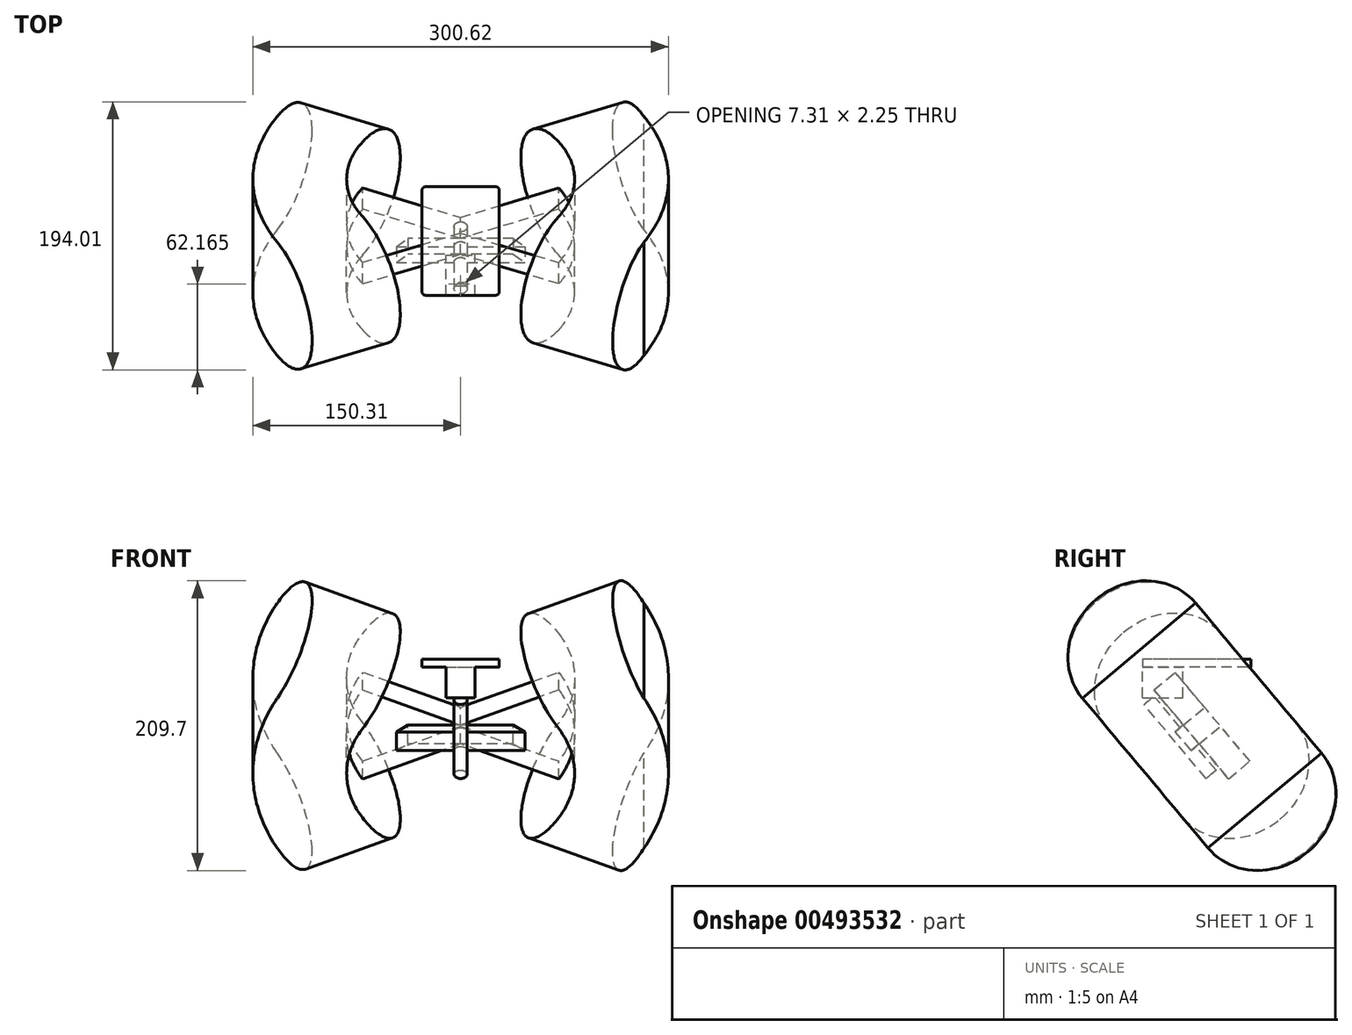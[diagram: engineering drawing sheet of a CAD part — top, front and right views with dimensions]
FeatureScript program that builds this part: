
annotation { "Feature Type Name" : "Feature", "Feature Type Description" : "" }
export const myFeature = defineFeature(function(context is Context, id is Id, definition is map)
    precondition{}
    {
        {
            var Q0;
            Q0=qCreatedBy(makeId("Top.planeOp"),FACE);
            var sketch = newSketch(context, id + "F0", { "sketchPlane" : qUnion([Q0])});
            skLineSegment(sketch, "E0.bottom", {"start": v(-25.4, 39.27) * mm, "end": v(25.4, 39.27) * mm});
            skLineSegment(sketch, "E0.top", {"start": v(-25.4, -39.27) * mm, "end": v(25.4, -39.27) * mm});
            skLineSegment(sketch, "E0.left", {"start": v(-27.94, 36.73) * mm, "end": v(-27.94, -36.73) * mm});
            skLineSegment(sketch, "E0.right", {"start": v(27.94, 36.73) * mm, "end": v(27.94, -36.73) * mm});
            skLineSegment(sketch, "E1", {"start": v(-27.94, 39.27) * mm, "end": v(27.94, -39.27) * mm, "construction": true});
            skPoint(sketch, "E2.visualSharp", {"position": v(-27.94, 39.27) * mm});
            skArc(sketch, "E2.filletArc", {"start": v(-25.4, 39.27) * mm, "mid": v(-27.2, 38.52) * mm, "end": v(-27.94, 36.73) * mm});
            skPoint(sketch, "E3.visualSharp", {"position": v(27.94, 39.27) * mm});
            skArc(sketch, "E3.filletArc", {"start": v(27.94, 36.73) * mm, "mid": v(27.2, 38.52) * mm, "end": v(25.4, 39.27) * mm});
            skPoint(sketch, "E4.visualSharp", {"position": v(27.94, -39.27) * mm});
            skArc(sketch, "E4.filletArc", {"start": v(25.4, -39.27) * mm, "mid": v(27.2, -38.52) * mm, "end": v(27.94, -36.73) * mm});
            skPoint(sketch, "E5.visualSharp", {"position": v(-27.94, -39.27) * mm});
            skArc(sketch, "E5.filletArc", {"start": v(-27.94, -36.73) * mm, "mid": v(-27.2, -38.52) * mm, "end": v(-25.4, -39.27) * mm});
            skSolve(sketch);
        }
        {
            var Q0;
            Q0 = qSketchRegion(id + "F0", true);
            extrude(context, id + "F1", {"entities" : qUnion([Q0]), "depth" : 5.64 * mm, "offsetDistance" : 25.4 * mm});
        }
        {
            var Q0;
            Q0=makeQuery(id+"F1.opExtrude","CAP_FACE",FACE,{"disambiguationData":[OSD([sQuery(id+"F0.wireOp",EDGE,"E0.bottom"),sQuery(id+"F0.wireOp",EDGE,"E0.top"),sQuery(id+"F0.wireOp",EDGE,"E0.left"),sQuery(id+"F0.wireOp",EDGE,"E0.right"),sQuery(id+"F0.wireOp",EDGE,"E2.filletArc"),sQuery(id+"F0.wireOp",EDGE,"E3.filletArc"),sQuery(id+"F0.wireOp",EDGE,"E4.filletArc"),sQuery(id+"F0.wireOp",EDGE,"E5.filletArc")])],"isStart":true});
            var sketch = newSketch(context, id + "F2", { "sketchPlane" : qUnion([Q0])});
            skLineSegment(sketch, "E6.bottom", {"start": v(-10.49, 39.27) * mm, "end": v(10.49, 39.27) * mm});
            skLineSegment(sketch, "E6.top", {"start": v(-10.49, 10.06) * mm, "end": v(10.49, 10.06) * mm});
            skLineSegment(sketch, "E6.left", {"start": v(-10.49, 39.27) * mm, "end": v(-10.49, 10.06) * mm});
            skLineSegment(sketch, "E6.right", {"start": v(10.49, 39.27) * mm, "end": v(10.49, 10.06) * mm});
            skLineSegment(sketch, "E7", {"start": v(0, 0) * mm, "end": v(0, 10.06) * mm, "construction": true});
            skSolve(sketch);
        }
        {
            var Q0;
            Q0 = qSketchRegion(id + "F2", true);
            extrude(context, id + "F3", {"entities" : qUnion([Q0]), "operationType" : NewBodyOperationType.ADD, "depth" : 22.22 * mm, "offsetDistance" : 25.4 * mm});
        }
        {
            var Q0;
            Q0=qCreatedBy(makeId("Right.planeOp"),FACE);
            var sketch = newSketch(context, id + "F4", { "sketchPlane" : qUnion([Q0])});
            skLineSegment(sketch, "E8", {"start": v(-39.27, -18.6) * mm, "end": v(10.3, -77.67) * mm, "construction": true});
            skLineSegment(sketch, "E9", {"start": v(-38.23, 0) * mm, "end": v(-38.23, -19.84) * mm, "construction": true});
            skLineSegment(sketch, "E10", {"start": v(-38.23, -19.84) * mm, "end": v(-39.27, -19.84) * mm, "construction": true});
            skLineSegment(sketch, "E11", {"start": v(-30.97, -21.12) * mm, "end": v(-38.23, -27.2) * mm, "construction": true});
            skPoint(sketch, "E12", {"position": v(-34.6, -24.16) * mm});
            skPoint(sketch, "E13", {"position": v(-15.5, -46.93) * mm});
            skPoint(sketch, "E14", {"position": v(-4.07, -60.55) * mm});
            skPoint(sketch, "E15", {"position": v(-9.78, -53.74) * mm});
            skLineSegment(sketch, "E16", {"start": v(-9.78, -53.74) * mm, "end": v(17.1, -31.18) * mm, "construction": true});
            skSolve(sketch);
        }
        {
            var Q0;
            Q0=sQuery(id+"F4.wireOp",EDGE,"E11");
            cPoint(context, id + "F5", {"entities" : qUnion([Q0]), "parameter" : 0.5});
        }
        {
            var Q0;
            Q0 = qCreatedBy(id + "F5" ,VERTEX);
            var Q1;
            Q1=sQuery(id+"F4.wireOp",EDGE,"E8");
            cPlane(context, id + "F6", {"entities" : qUnion([Q0, Q1]), "cplaneType" : CPlaneType.LINE_POINT, "offset" : 25.4 * mm, "width" : 152.4 * mm, "height" : 152.4 * mm});
        }
        {
            var Q0;
            Q0=qCreatedBy(id+"F6.planeOp",FACE);
            var sketch = newSketch(context, id + "F7", { "sketchPlane" : qUnion([Q0])});
            skCircle(sketch, "E17", {"center": v(0, 42.03) * mm, "radius": 4.74 * mm});
            skSolve(sketch);
        }
        {
            var Q0;
            Q0 = qSketchRegion(id + "F7", true);
            var Q1;
            Q1=sQuery(id+"F4.wireOp",VERTEX,"E8.end");
            extrude(context, id + "F8", {"entities" : qUnion([Q0]), "operationType" : NewBodyOperationType.ADD, "endBound" : BoundingType.UP_TO_VERTEX, "depth" : 25.4 * mm, "endBoundEntityVertex" : qUnion([Q1]), "offsetDistance" : 25.4 * mm});
        }
        {
            var Q0;
            Q0=sQuery(id+"F4.wireOp",EDGE,"E8");
            var Q1;
            Q1=sQuery(id+"F4.wireOp",VERTEX,"E13");
            cPlane(context, id + "F9", {"entities" : qUnion([Q0, Q1]), "cplaneType" : CPlaneType.LINE_POINT, "offset" : 25.4 * mm, "width" : 152.4 * mm, "height" : 152.4 * mm});
        }
        {
            var Q0;
            Q0=qCreatedBy(id+"F9.planeOp",FACE);
            var sketch = newSketch(context, id + "F10", { "sketchPlane" : qUnion([Q0])});
            skLineSegment(sketch, "E18", {"start": v(-92, 14.45) * mm, "end": v(92, 14.45) * mm});
            skLineSegment(sketch, "E19", {"start": v(92, 14.45) * mm, "end": v(92, 34.47) * mm});
            skLineSegment(sketch, "E20", {"start": v(92, 34.47) * mm, "end": v(-92, 34.47) * mm});
            skLineSegment(sketch, "E21", {"start": v(-92, 34.47) * mm, "end": v(-92, 14.45) * mm});
            skLineSegment(sketch, "E22", {"start": v(0, 34.47) * mm, "end": v(0, 0) * mm, "construction": true});
            skLineSegment(sketch, "E23", {"start": v(-46.47, 42.03) * mm, "end": v(-38.1, 34.47) * mm});
            skLineSegment(sketch, "E24", {"start": v(-46.47, 42.03) * mm, "end": v(46.47, 42.03) * mm});
            skLineSegment(sketch, "E25", {"start": v(38.1, 34.47) * mm, "end": v(46.47, 42.03) * mm});
            skSolve(sketch);
        }
        {
            var Q0;
            Q0 = qSketchRegion(id + "F10", true);
            var Q1;
            Q1=sQuery(id+"F4.wireOp",VERTEX,"E14");
            extrude(context, id + "F11", {"entities" : qUnion([Q0]), "operationType" : NewBodyOperationType.ADD, "endBound" : BoundingType.UP_TO_VERTEX, "depth" : 25.4 * mm, "endBoundEntityVertex" : qUnion([Q1]), "offsetDistance" : 25.4 * mm});
        }
        {
            var Q0;
            Q0=makeQuery(id+"F11.opExtrude","SWEPT_FACE",FACE,{"disambiguationData":[OSD([sQuery(id+"F10.wireOp",EDGE,"E18")])]});
            var sketch = newSketch(context, id + "F12", { "sketchPlane" : qUnion([Q0])});
            skArc(sketch, "E26", {"start": v(-80.04, 11.34) * mm, "mid": v(-92.43, -34.88) * mm, "end": v(-80.04, -81.1) * mm});
            skLineSegment(sketch, "E27", {"start": v(0, -25.99) * mm, "end": v(80.04, 11.34) * mm});
            skLineSegment(sketch, "E28", {"start": v(0, -25.99) * mm, "end": v(-80.04, 11.34) * mm});
            skLineSegment(sketch, "E29", {"start": v(0, -43.77) * mm, "end": v(-80.04, -81.1) * mm});
            skLineSegment(sketch, "E30", {"start": v(80.04, -81.1) * mm, "end": v(0, -43.77) * mm});
            skArc(sketch, "E31.trimOffspring", {"start": v(80.04, -81.1) * mm, "mid": v(92.43, -34.88) * mm, "end": v(80.04, 11.34) * mm});
            skLineSegment(sketch, "E32", {"start": v(92, -34.88) * mm, "end": v(-92, -34.88) * mm, "construction": true});
            skLineSegment(sketch, "E33.bottom", {"start": v(-140.46, 18.63) * mm, "end": v(-82.47, 18.63) * mm, "construction": true});
            skLineSegment(sketch, "E33.top", {"start": v(-140.46, -88.38) * mm, "end": v(-82.47, -88.38) * mm, "construction": true});
            skLineSegment(sketch, "E33.left", {"start": v(-140.46, 18.63) * mm, "end": v(-140.46, -88.38) * mm, "construction": true});
            skLineSegment(sketch, "E33.right", {"start": v(-82.47, 18.63) * mm, "end": v(-82.47, -88.38) * mm, "construction": true});
            skPoint(sketch, "E34", {"position": v(-82.47, -34.88) * mm});
            skArc(sketch, "E35", {"start": v(-132.62, 35.86) * mm, "mid": v(-150.3, -34.88) * mm, "end": v(-132.62, -105.61) * mm});
            skLineSegment(sketch, "E36", {"start": v(-80.04, 11.34) * mm, "end": v(-132.62, 35.86) * mm, "construction": true});
            skLineSegment(sketch, "E37", {"start": v(-80.04, -81.1) * mm, "end": v(-132.62, -105.61) * mm, "construction": true});
            skLineSegment(sketch, "E38", {"start": v(80.04, 11.34) * mm, "end": v(132.62, 35.86) * mm, "construction": true});
            skLineSegment(sketch, "E39", {"start": v(80.04, -81.1) * mm, "end": v(132.62, -105.61) * mm, "construction": true});
            skArc(sketch, "E40", {"start": v(-70.98, 7.11) * mm, "mid": v(-82.47, -34.88) * mm, "end": v(-70.98, -76.87) * mm});
            skLineSegment(sketch, "E41", {"start": v(-110.03, 84.31) * mm, "end": v(-43.63, 53.35) * mm});
            skLineSegment(sketch, "E42", {"start": v(43.63, 53.35) * mm, "end": v(107.43, 83.1) * mm});
            skLineSegment(sketch, "E43", {"start": v(-110.03, -154.07) * mm, "end": v(-43.63, -123.1) * mm});
            skLineSegment(sketch, "E44", {"start": v(43.63, -123.1) * mm, "end": v(107.43, -152.86) * mm});
            skArc(sketch, "E45.trimOffspring", {"start": v(70.98, -76.87) * mm, "mid": v(82.47, -34.88) * mm, "end": v(70.98, 7.11) * mm});
            skArc(sketch, "E46.trimOffspring", {"start": v(132.62, -105.61) * mm, "mid": v(150.3, -34.88) * mm, "end": v(132.62, 35.86) * mm});
            skLineSegment(sketch, "E47", {"start": v(-70.98, 7.11) * mm, "end": v(-43.63, 53.35) * mm});
            skLineSegment(sketch, "E48", {"start": v(-132.62, 35.86) * mm, "end": v(-110.03, 84.31) * mm});
            skLineSegment(sketch, "E49", {"start": v(-132.62, -105.61) * mm, "end": v(-110.03, -154.07) * mm});
            skLineSegment(sketch, "E50", {"start": v(-70.98, -76.87) * mm, "end": v(-43.63, -123.1) * mm});
            skLineSegment(sketch, "E51", {"start": v(70.98, 7.11) * mm, "end": v(43.63, 53.35) * mm});
            skLineSegment(sketch, "E52", {"start": v(132.62, 35.86) * mm, "end": v(107.43, 83.1) * mm});
            skLineSegment(sketch, "E53", {"start": v(70.98, -76.87) * mm, "end": v(43.63, -123.1) * mm});
            skLineSegment(sketch, "E54", {"start": v(132.62, -105.61) * mm, "end": v(107.43, -152.86) * mm});
            skSolve(sketch);
        }
        {
            var Q0;
            {var subQ0=sQuery(id+"F12.wireOp",EDGE,"E28");var subQ3=sQuery(id+"F12.wireOp",EDGE,"E40");var subQ4=makeQuery(id+"F12.imprint","INTERSECT",VERTEX,{"derivedFrom":[subQ0,subQ3]});Q0=makeQuery(id+"F12.imprint","IMPRINT",FACE,{"disambiguationData":[TD([[makeQuery(id+"F12.imprint","IMPRINT",EDGE,{"disambiguationData":[TD([[subQ4,-1.0]])],"derivedFrom":subQ3}),1.0]])]});}
            var Q1;
            {var subQ0=sQuery(id+"F12.wireOp",EDGE,"E26");var subQ4=sQuery(id+"F12.wireOp",EDGE,"E28");var subQ5=makeQuery(id+"F12.imprint","INTERSECT",VERTEX,{"derivedFrom":[subQ0,subQ4]});Q1=makeQuery(id+"F12.imprint","IMPRINT",FACE,{"disambiguationData":[TD([[makeQuery(id+"F12.imprint","IMPRINT",EDGE,{"disambiguationData":[TD([[subQ5,1.0]])],"derivedFrom":subQ4}),1.0]])]});}
            var Q2;
            {var subQ0=sQuery(id+"F12.wireOp",EDGE,"E29");var subQ3=sQuery(id+"F12.wireOp",EDGE,"E40");var subQ4=makeQuery(id+"F12.imprint","INTERSECT",VERTEX,{"derivedFrom":[subQ0,subQ3]});Q2=makeQuery(id+"F12.imprint","IMPRINT",FACE,{"disambiguationData":[TD([[makeQuery(id+"F12.imprint","IMPRINT",EDGE,{"disambiguationData":[TD([[subQ4,1.0]])],"derivedFrom":subQ3}),1.0]])]});}
            var Q3;
            {var subQ0=sQuery(id+"F12.wireOp",EDGE,"E26");var subQ4=sQuery(id+"F12.wireOp",EDGE,"E29");var subQ5=makeQuery(id+"F12.imprint","INTERSECT",VERTEX,{"derivedFrom":[subQ0,subQ4]});Q3=makeQuery(id+"F12.imprint","IMPRINT",FACE,{"disambiguationData":[TD([[makeQuery(id+"F12.imprint","IMPRINT",EDGE,{"disambiguationData":[TD([[subQ5,1.0]])],"derivedFrom":subQ4}),-1.0]])]});}
            var Q4;
            {var subQ0=sQuery(id+"F12.wireOp",EDGE,"E27");var subQ3=sQuery(id+"F12.wireOp",EDGE,"E45.trimOffspring");var subQ4=makeQuery(id+"F12.imprint","INTERSECT",VERTEX,{"derivedFrom":[subQ0,subQ3]});Q4=makeQuery(id+"F12.imprint","IMPRINT",FACE,{"disambiguationData":[TD([[makeQuery(id+"F12.imprint","IMPRINT",EDGE,{"disambiguationData":[TD([[subQ4,1.0]])],"derivedFrom":subQ3}),1.0]])]});}
            var Q5;
            {var subQ0=sQuery(id+"F12.wireOp",EDGE,"E31.trimOffspring");var subQ1=sQuery(id+"F12.wireOp",EDGE,"E27");var subQ2=makeQuery(id+"F12.imprint","INTERSECT",VERTEX,{"derivedFrom":[subQ1,subQ0]});Q5=makeQuery(id+"F12.imprint","IMPRINT",FACE,{"disambiguationData":[TD([[makeQuery(id+"F12.imprint","IMPRINT",EDGE,{"disambiguationData":[TD([[subQ2,1.0]])],"derivedFrom":subQ1}),-1.0]])]});}
            var Q6;
            {var subQ0=sQuery(id+"F12.wireOp",EDGE,"E30");var subQ3=sQuery(id+"F12.wireOp",EDGE,"E45.trimOffspring");var subQ4=makeQuery(id+"F12.imprint","INTERSECT",VERTEX,{"derivedFrom":[subQ0,subQ3]});Q6=makeQuery(id+"F12.imprint","IMPRINT",FACE,{"disambiguationData":[TD([[makeQuery(id+"F12.imprint","IMPRINT",EDGE,{"disambiguationData":[TD([[subQ4,-1.0]])],"derivedFrom":subQ3}),1.0]])]});}
            var Q7;
            {var subQ0=sQuery(id+"F12.wireOp",EDGE,"E31.trimOffspring");var subQ1=sQuery(id+"F12.wireOp",EDGE,"E30");var subQ2=makeQuery(id+"F12.imprint","INTERSECT",VERTEX,{"derivedFrom":[subQ1,subQ0]});Q7=makeQuery(id+"F12.imprint","IMPRINT",FACE,{"disambiguationData":[TD([[makeQuery(id+"F12.imprint","IMPRINT",EDGE,{"disambiguationData":[TD([[subQ2,-1.0]])],"derivedFrom":subQ1}),-1.0]])]});}
            var Q8;
            {var subQ0=sQuery(id+"F10.wireOp",EDGE,"E20");Q8=makeQuery(id+"F11.opExtrude","SWEPT_FACE",FACE,{"disambiguationData":[OSD([subQ0]),TDD([makeQuery(id+"F10.imprint","IMPRINT",EDGE,{"disambiguationData":[TD([[makeQuery(id+"F10.imprint","INTERSECT",VERTEX,{"derivedFrom":[subQ0,sQuery(id+"F10.wireOp",EDGE,"E21")]}),1.0]])],"derivedFrom":subQ0})])]});}
            extrude(context, id + "F13", {"entities" : qUnion([Q0, Q1, Q2, Q3, Q4, Q5, Q6, Q7]), "operationType" : NewBodyOperationType.ADD, "endBound" : BoundingType.UP_TO_SURFACE, "oppositeDirection" : true, "depth" : 25.4 * mm, "endBoundEntityFace" : qUnion([Q8]), "offsetDistance" : 25.4 * mm});
        }
        {
            var Q0;
            Q0=makeQuery(id+"F12.imprint","IMPRINT",FACE,{"disambiguationData":[TD([[makeQuery(id+"F12.imprint","IMPRINT",EDGE,{"derivedFrom":sQuery(id+"F12.wireOp",EDGE,"E35")}),1.0]])]});
            var Q1;
            {var subQ13=sQuery(id+"F12.wireOp",EDGE,"E42");Q1=makeQuery(id+"F12.imprint","IMPRINT",FACE,{"disambiguationData":[TD([[makeQuery(id+"F12.imprint","IMPRINT",EDGE,{"derivedFrom":subQ13}),-1.0]])]});}
            var Q2;
            {var subQ0=sQuery(id+"F12.wireOp",EDGE,"E26");var subQ4=sQuery(id+"F12.wireOp",EDGE,"E28");var subQ5=makeQuery(id+"F12.imprint","INTERSECT",VERTEX,{"derivedFrom":[subQ0,subQ4]});Q2=makeQuery(id+"F12.imprint","IMPRINT",FACE,{"disambiguationData":[TD([[makeQuery(id+"F12.imprint","IMPRINT",EDGE,{"disambiguationData":[TD([[subQ5,1.0]])],"derivedFrom":subQ4}),1.0]])]});}
            var Q3;
            {var subQ1=sQuery(id+"F10.wireOp",EDGE,"E18");var subQ6=makeQuery(id+"F11.opExtrude","SWEPT_EDGE",EDGE,{"disambiguationData":[OSD([subQ1,sQuery(id+"F10.wireOp",EDGE,"E19")])]});Q3=makeQuery(id+"F12.imprint","IMPRINT",FACE,{"disambiguationData":[TD([[makeQuery(id+"F12.imprint","IMPRINT",EDGE,{"derivedFrom":subQ6}),-1.0]])]});}
            var Q4;
            {var subQ0=sQuery(id+"F12.wireOp",EDGE,"E26");var subQ4=sQuery(id+"F12.wireOp",EDGE,"E29");var subQ5=makeQuery(id+"F12.imprint","INTERSECT",VERTEX,{"derivedFrom":[subQ0,subQ4]});Q4=makeQuery(id+"F12.imprint","IMPRINT",FACE,{"disambiguationData":[TD([[makeQuery(id+"F12.imprint","IMPRINT",EDGE,{"disambiguationData":[TD([[subQ5,1.0]])],"derivedFrom":subQ4}),-1.0]])]});}
            var Q5;
            {var subQ0=sQuery(id+"F12.wireOp",EDGE,"E31.trimOffspring");var subQ1=sQuery(id+"F12.wireOp",EDGE,"E27");var subQ2=makeQuery(id+"F12.imprint","INTERSECT",VERTEX,{"derivedFrom":[subQ1,subQ0]});Q5=makeQuery(id+"F12.imprint","IMPRINT",FACE,{"disambiguationData":[TD([[makeQuery(id+"F12.imprint","IMPRINT",EDGE,{"disambiguationData":[TD([[subQ2,1.0]])],"derivedFrom":subQ1}),-1.0]])]});}
            var Q6;
            {var subQ1=sQuery(id+"F10.wireOp",EDGE,"E18");var subQ6=makeQuery(id+"F11.opExtrude","SWEPT_EDGE",EDGE,{"disambiguationData":[OSD([subQ1,sQuery(id+"F10.wireOp",EDGE,"E21")])]});Q6=makeQuery(id+"F12.imprint","IMPRINT",FACE,{"disambiguationData":[TD([[makeQuery(id+"F12.imprint","IMPRINT",EDGE,{"derivedFrom":subQ6}),1.0]])]});}
            var Q7;
            {var subQ0=sQuery(id+"F12.wireOp",EDGE,"E31.trimOffspring");var subQ1=sQuery(id+"F12.wireOp",EDGE,"E30");var subQ2=makeQuery(id+"F12.imprint","INTERSECT",VERTEX,{"derivedFrom":[subQ1,subQ0]});Q7=makeQuery(id+"F12.imprint","IMPRINT",FACE,{"disambiguationData":[TD([[makeQuery(id+"F12.imprint","IMPRINT",EDGE,{"disambiguationData":[TD([[subQ2,-1.0]])],"derivedFrom":subQ1}),-1.0]])]});}
            var Q8;
            {var subQ1=sQuery(id+"F10.wireOp",EDGE,"E18");var subQ2=makeQuery(id+"F11.opExtrude","SWEPT_EDGE",EDGE,{"disambiguationData":[OSD([subQ1,sQuery(id+"F10.wireOp",EDGE,"E21")])]});Q8=makeQuery(id+"F12.imprint","IMPRINT",FACE,{"disambiguationData":[TD([[makeQuery(id+"F12.imprint","IMPRINT",EDGE,{"derivedFrom":subQ2}),-1.0]])]});}
            var Q9;
            {var subQ1=sQuery(id+"F10.wireOp",EDGE,"E18");var subQ2=makeQuery(id+"F11.opExtrude","SWEPT_EDGE",EDGE,{"disambiguationData":[OSD([subQ1,sQuery(id+"F10.wireOp",EDGE,"E19")])]});Q9=makeQuery(id+"F12.imprint","IMPRINT",FACE,{"disambiguationData":[TD([[makeQuery(id+"F12.imprint","IMPRINT",EDGE,{"derivedFrom":subQ2}),1.0]])]});}
            extrude(context, id + "F14", {"entities" : qUnion([Q0, Q1, Q2, Q3, Q4, Q5, Q6, Q7, Q8, Q9]), "operationType" : NewBodyOperationType.ADD, "oppositeDirection" : true, "depth" : 63.53 * mm, "offsetDistance" : 25.4 * mm});
        }
        {
            var Q0;
            {var subQ13=sQuery(id+"F12.wireOp",EDGE,"E42");Q0=makeQuery(id+"F12.imprint","IMPRINT",FACE,{"disambiguationData":[TD([[makeQuery(id+"F12.imprint","IMPRINT",EDGE,{"derivedFrom":subQ13}),-1.0]])]});}
            var Q1;
            Q1=makeQuery(id+"F12.imprint","IMPRINT",FACE,{"disambiguationData":[TD([[makeQuery(id+"F12.imprint","IMPRINT",EDGE,{"derivedFrom":sQuery(id+"F12.wireOp",EDGE,"E35")}),1.0]])]});
            var Q2;
            {var subQ0=sQuery(id+"F12.wireOp",EDGE,"E26");var subQ4=sQuery(id+"F12.wireOp",EDGE,"E28");var subQ5=makeQuery(id+"F12.imprint","INTERSECT",VERTEX,{"derivedFrom":[subQ0,subQ4]});Q2=makeQuery(id+"F12.imprint","IMPRINT",FACE,{"disambiguationData":[TD([[makeQuery(id+"F12.imprint","IMPRINT",EDGE,{"disambiguationData":[TD([[subQ5,1.0]])],"derivedFrom":subQ4}),1.0]])]});}
            var Q3;
            {var subQ0=sQuery(id+"F12.wireOp",EDGE,"E26");var subQ4=sQuery(id+"F12.wireOp",EDGE,"E29");var subQ5=makeQuery(id+"F12.imprint","INTERSECT",VERTEX,{"derivedFrom":[subQ0,subQ4]});Q3=makeQuery(id+"F12.imprint","IMPRINT",FACE,{"disambiguationData":[TD([[makeQuery(id+"F12.imprint","IMPRINT",EDGE,{"disambiguationData":[TD([[subQ5,1.0]])],"derivedFrom":subQ4}),-1.0]])]});}
            var Q4;
            {var subQ1=sQuery(id+"F10.wireOp",EDGE,"E18");var subQ6=makeQuery(id+"F11.opExtrude","SWEPT_EDGE",EDGE,{"disambiguationData":[OSD([subQ1,sQuery(id+"F10.wireOp",EDGE,"E19")])]});Q4=makeQuery(id+"F12.imprint","IMPRINT",FACE,{"disambiguationData":[TD([[makeQuery(id+"F12.imprint","IMPRINT",EDGE,{"derivedFrom":subQ6}),-1.0]])]});}
            var Q5;
            {var subQ0=sQuery(id+"F12.wireOp",EDGE,"E31.trimOffspring");var subQ1=sQuery(id+"F12.wireOp",EDGE,"E27");var subQ2=makeQuery(id+"F12.imprint","INTERSECT",VERTEX,{"derivedFrom":[subQ1,subQ0]});Q5=makeQuery(id+"F12.imprint","IMPRINT",FACE,{"disambiguationData":[TD([[makeQuery(id+"F12.imprint","IMPRINT",EDGE,{"disambiguationData":[TD([[subQ2,1.0]])],"derivedFrom":subQ1}),-1.0]])]});}
            var Q6;
            {var subQ1=sQuery(id+"F10.wireOp",EDGE,"E18");var subQ6=makeQuery(id+"F11.opExtrude","SWEPT_EDGE",EDGE,{"disambiguationData":[OSD([subQ1,sQuery(id+"F10.wireOp",EDGE,"E21")])]});Q6=makeQuery(id+"F12.imprint","IMPRINT",FACE,{"disambiguationData":[TD([[makeQuery(id+"F12.imprint","IMPRINT",EDGE,{"derivedFrom":subQ6}),1.0]])]});}
            var Q7;
            {var subQ0=sQuery(id+"F12.wireOp",EDGE,"E31.trimOffspring");var subQ1=sQuery(id+"F12.wireOp",EDGE,"E30");var subQ2=makeQuery(id+"F12.imprint","INTERSECT",VERTEX,{"derivedFrom":[subQ1,subQ0]});Q7=makeQuery(id+"F12.imprint","IMPRINT",FACE,{"disambiguationData":[TD([[makeQuery(id+"F12.imprint","IMPRINT",EDGE,{"disambiguationData":[TD([[subQ2,-1.0]])],"derivedFrom":subQ1}),-1.0]])]});}
            var Q8;
            {var subQ1=sQuery(id+"F10.wireOp",EDGE,"E18");var subQ2=makeQuery(id+"F11.opExtrude","SWEPT_EDGE",EDGE,{"disambiguationData":[OSD([subQ1,sQuery(id+"F10.wireOp",EDGE,"E21")])]});Q8=makeQuery(id+"F12.imprint","IMPRINT",FACE,{"disambiguationData":[TD([[makeQuery(id+"F12.imprint","IMPRINT",EDGE,{"derivedFrom":subQ2}),-1.0]])]});}
            var Q9;
            {var subQ1=sQuery(id+"F10.wireOp",EDGE,"E18");var subQ2=makeQuery(id+"F11.opExtrude","SWEPT_EDGE",EDGE,{"disambiguationData":[OSD([subQ1,sQuery(id+"F10.wireOp",EDGE,"E19")])]});Q9=makeQuery(id+"F12.imprint","IMPRINT",FACE,{"disambiguationData":[TD([[makeQuery(id+"F12.imprint","IMPRINT",EDGE,{"derivedFrom":subQ2}),1.0]])]});}
            extrude(context, id + "F15", {"entities" : qUnion([Q0, Q1, Q2, Q3, Q4, Q5, Q6, Q7, Q8, Q9]), "operationType" : NewBodyOperationType.ADD, "depth" : 43.5 * mm, "offsetDistance" : 25.4 * mm});
        }
        {
            var Q0;
            Q0=makeQuery(id+"F14.opExtrude","CAP_EDGE",EDGE,{"disambiguationData":[OSD([sQuery(id+"F12.wireOp",EDGE,"E42")])],"isStart":false});
            var Q1;
            Q1=makeQuery(id+"F15.opExtrude","CAP_EDGE",EDGE,{"disambiguationData":[OSD([sQuery(id+"F12.wireOp",EDGE,"E42")])],"isStart":false});
            var Q2;
            Q2=makeQuery(id+"F14.opExtrude","CAP_EDGE",EDGE,{"disambiguationData":[OSD([sQuery(id+"F12.wireOp",EDGE,"E41")])],"isStart":false});
            var Q3;
            Q3=makeQuery(id+"F15.opExtrude","CAP_EDGE",EDGE,{"disambiguationData":[OSD([sQuery(id+"F12.wireOp",EDGE,"E41")])],"isStart":false});
            var Q4;
            Q4=makeQuery(id+"F15.opExtrude","CAP_EDGE",EDGE,{"disambiguationData":[OSD([sQuery(id+"F12.wireOp",EDGE,"E43")])],"isStart":false});
            var Q5;
            Q5=makeQuery(id+"F14.opExtrude","CAP_EDGE",EDGE,{"disambiguationData":[OSD([sQuery(id+"F12.wireOp",EDGE,"E43")])],"isStart":false});
            var Q6;
            Q6=makeQuery(id+"F15.opExtrude","CAP_EDGE",EDGE,{"disambiguationData":[OSD([sQuery(id+"F12.wireOp",EDGE,"E44")])],"isStart":false});
            var Q7;
            Q7=makeQuery(id+"F14.opExtrude","CAP_EDGE",EDGE,{"disambiguationData":[OSD([sQuery(id+"F12.wireOp",EDGE,"E44")])],"isStart":false});
            fillet(context, id + "F16", {"entities" : qUnion([Q0, Q1, Q2, Q3, Q4, Q5, Q6, Q7]), "tangentPropagation" : true, "radius" : 53.34 * mm, "defaultsChanged" : false, "vertexSettings" : [], "allowEdgeOverflow" : false});
        }
        {
            var Q0;
            Q0=makeQuery(id+"F1.opExtrude","SWEPT_BODY",BODY,{"disambiguationData":[OSD([sQuery(id+"F0.wireOp",EDGE,"E0.bottom"),sQuery(id+"F0.wireOp",EDGE,"E0.top"),sQuery(id+"F0.wireOp",EDGE,"E0.left"),sQuery(id+"F0.wireOp",EDGE,"E0.right"),sQuery(id+"F0.wireOp",EDGE,"E2.filletArc"),sQuery(id+"F0.wireOp",EDGE,"E3.filletArc"),sQuery(id+"F0.wireOp",EDGE,"E4.filletArc"),sQuery(id+"F0.wireOp",EDGE,"E5.filletArc")])]});
            transform(context, id + "F17", {"entities" : qUnion([Q0]), "transformType" : TransformType.TRANSLATION_3D, "dx" : 0 * mm, "dy" : 0 * mm, "dz" : 0 * mm, "makeCopy" : true});
        }
    });
